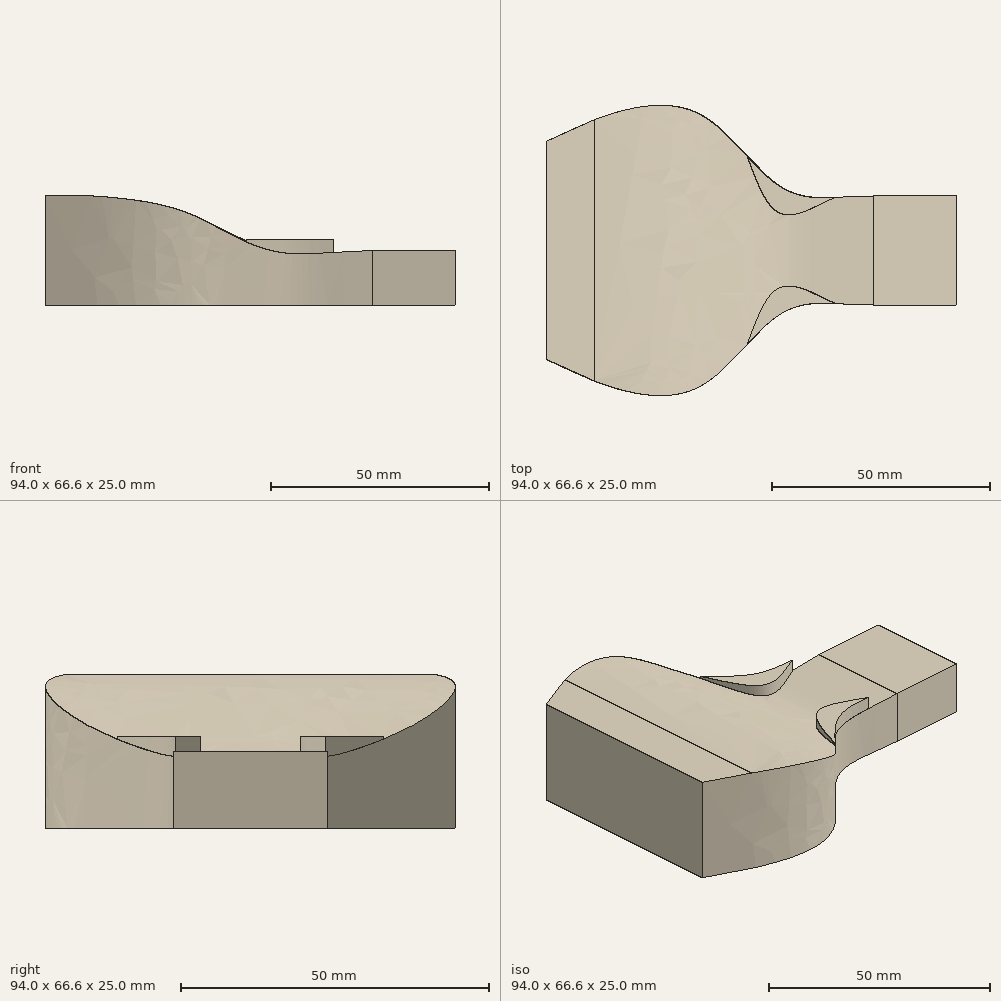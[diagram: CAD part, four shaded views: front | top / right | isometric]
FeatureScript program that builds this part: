
annotation { "Feature Type Name" : "Feature", "Feature Type Description" : "" }
export const myFeature = defineFeature(function(context is Context, id is Id, definition is map)
    precondition{}
    {
        {
            var Q0;
            Q0=qCreatedBy(makeId("Top.planeOp"),FACE);
            var sketch = newSketch(context, id + "F0", { "sketchPlane" : qUnion([Q0])});
            skLineSegment(sketch, "E0", {"start": v(-32.15, 0) * mm, "end": v(-32.15, 25) * mm});
            skLineSegment(sketch, "E1", {"start": v(42.85, 0) * mm, "end": v(42.85, 12.5) * mm});
            skFitSpline(sketch, "E2", {"points": [v(-32.15, 25) * mm, v(-16.91, 31.43) * mm, v(2.7, 31.43) * mm, v(22.53, 14.05) * mm, v(42.85, 12.5) * mm], "startDerivative": vector(94.79, 43.23) * mm, "endDerivative": vector(92.27, -1.18) * mm});
            skFitSpline(sketch, "E3.MirrorCS", {"points": [v(-32.15, -25) * mm, v(-16.91, -31.43) * mm, v(2.7, -31.43) * mm, v(22.53, -14.05) * mm, v(42.85, -12.5) * mm], "startDerivative": vector(94.79, -43.23) * mm, "endDerivative": vector(92.27, 1.18) * mm});
            skLineSegment(sketch, "E4.MirrorCS", {"start": v(-32.15, 0) * mm, "end": v(-32.15, -25) * mm});
            skLineSegment(sketch, "E5.MirrorCS", {"start": v(42.85, 0) * mm, "end": v(42.85, -12.5) * mm});
            skSolve(sketch);
        }
        {
            var Q0;
            Q0=makeQuery(id+"F0.imprint","IMPRINT",FACE,{"disambiguationData":[TD([[makeQuery(id+"F0.imprint","IMPRINT",EDGE,{"derivedFrom":sQuery(id+"F0.wireOp",EDGE,"E0")}),-1.0]])]});
            extrude(context, id + "F1", {"entities" : qUnion([Q0]), "depth" : 25 * mm});
        }
        {
            var Q0;
            Q0=qCreatedBy(makeId("Front.planeOp"),FACE);
            var sketch = newSketch(context, id + "F2", { "sketchPlane" : qUnion([Q0])});
            skLineSegment(sketch, "E6.0", {"start": v(-32.15, 25) * mm, "end": v(-32.15, 0) * mm});
            skLineSegment(sketch, "E7", {"start": v(42.85, 0) * mm, "end": v(42.85, 12.5) * mm});
            skFitSpline(sketch, "E8", {"points": [v(42.85, 12.5) * mm, v(30.39, 11.85) * mm, v(20.57, 12.29) * mm, v(10.27, 16.21) * mm, v(-3.97, 22.56) * mm, v(-32.15, 25) * mm], "startDerivative": vector(-65.38, -2.17) * mm, "endDerivative": vector(-72.27, -5.88) * mm});
            skLineSegment(sketch, "E9", {"start": v(42.85, 0) * mm, "end": v(-32.15, 0) * mm});
            skSolve(sketch);
        }
        {
            var Q0;
            Q0 = qSketchRegion(id + "F2", true);
            extrude(context, id + "F3", {"entities" : qUnion([Q0]), "operationType" : NewBodyOperationType.INTERSECT, "endBound" : BoundingType.SYMMETRIC, "depth" : 88.46 * mm});
        }
        {
            var Q0;
            Q0=qCreatedBy(makeId("Top.planeOp"),FACE);
            var sketch = newSketch(context, id + "F4", { "sketchPlane" : qUnion([Q0])});
            skFitSpline(sketch, "E10.0", {"points": [v(-32.15, 25) * mm, v(-25.07, 28.23) * mm, v(-18.53, 31.71) * mm, v(5.25, 36.39) * mm, v(20.78, 8.87) * mm, v(35.2, 12.6) * mm, v(42.85, 12.5) * mm]});
            skFitSpline(sketch, "E11", {"points": [v(-32.15, 25) * mm, v(-34, 32.96) * mm, v(-32.7, 43.34) * mm, v(-33.56, 51.35) * mm, v(-35.72, 58.05) * mm], "startDerivative": vector(-15.67, 34.06) * mm, "endDerivative": vector(-6.75, 15.63) * mm});
            skFitSpline(sketch, "E12", {"points": [v(-35.72, 58.05) * mm, v(-23.17, 60) * mm, v(-6.08, 53.94) * mm, v(5.39, 54.16) * mm], "startDerivative": vector(37.63, 12.7) * mm, "endDerivative": vector(35.9, 6.15) * mm});
            skFitSpline(sketch, "E13", {"points": [v(5.39, 54.16) * mm, v(7.98, 46.15) * mm, v(7.55, 40.1) * mm, v(5.39, 33.6) * mm, v(8.62, 26.19) * mm], "startDerivative": vector(12.12, -30.8) * mm, "endDerivative": vector(18.55, -28.53) * mm});
            skFitSpline(sketch, "E14.0", {"points": [v(42.85, 12.5) * mm, v(41.3, 12.52) * mm, v(38.23, 12.4) * mm, v(34.4, 12.15) * mm, v(31.32, 12.1) * mm, v(29, 12.19) * mm, v(27.12, 12.45) * mm, v(25.63, 12.8) * mm, v(24.71, 13.09) * mm, v(23.99, 13.36) * mm, v(23.28, 13.67) * mm, v(22.43, 14.1) * mm, v(21.46, 14.67) * mm, v(20.53, 15.32) * mm, v(19.64, 16) * mm, v(18.48, 16.98) * mm, v(17.11, 18.26) * mm, v(15.55, 19.85) * mm, v(13.54, 22) * mm, v(11.56, 24.15) * mm, v(9.55, 26.2) * mm, v(8, 27.67) * mm, v(6.4, 29.05) * mm, v(4.97, 30.1) * mm, v(3.75, 30.87) * mm, v(2.5, 31.56) * mm, v(1.2, 32.12) * mm, v(-0.18, 32.56) * mm, v(-1.25, 32.83) * mm, v(-2.35, 33.03) * mm, v(-3.81, 33.23) * mm, v(-5.3, 33.31) * mm, v(-6.81, 33.3) * mm, v(-8.34, 33.21) * mm, v(-10.23, 33) * mm, v(-12.47, 32.6) * mm, v(-14.7, 32.08) * mm, v(-16.9, 31.45) * mm, v(-19.1, 30.74) * mm, v(-20.54, 30.2) * mm, v(-21.26, 29.9) * mm]});
            skPoint(sketch, "E15.orphan", {"position": v(42.85, 12.5) * mm});
            skSolve(sketch);
        }
        {
            var Q0;
            Q0=makeQuery(id+"F4.imprint","IMPRINT",FACE,{"disambiguationData":[TD([[makeQuery(id+"F4.imprint","IMPRINT",EDGE,{"derivedFrom":sQuery(id+"F4.wireOp",EDGE,"E10.0")}),1.0]])]});
            extrude(context, id + "F5", {"entities" : qUnion([Q0]), "depth" : 15 * mm});
        }
        {
            var Q0;
            Q0=makeQuery(id+"F5.opExtrude","SWEPT_BODY",BODY,{"disambiguationData":[OSD([sQuery(id+"F4.wireOp",EDGE,"E10.0"),sQuery(id+"F4.wireOp",EDGE,"E11"),sQuery(id+"F4.wireOp",EDGE,"E12"),sQuery(id+"F4.wireOp",EDGE,"E13"),sQuery(id+"F4.wireOp",EDGE,"E14.0")])]});
            var Q1;
            Q1=qCreatedBy(makeId("Front.planeOp"),FACE);
            mirror(context, id + "F6", {"entities" : qUnion([Q0]), "mirrorPlane" : qUnion([Q1])});
        }
        {
            var Q0;
            Q0=makeQuery(id+"F1.opExtrude","SWEPT_BODY",BODY,{"disambiguationData":[OSD([sQuery(id+"F0.wireOp",EDGE,"E0"),sQuery(id+"F0.wireOp",EDGE,"E1"),sQuery(id+"F0.wireOp",EDGE,"E2"),sQuery(id+"F0.wireOp",EDGE,"E3.MirrorCS"),sQuery(id+"F0.wireOp",EDGE,"E4.MirrorCS"),sQuery(id+"F0.wireOp",EDGE,"E5.MirrorCS")])]});
            var Q1;
            Q1=makeQuery(id+"F5.opExtrude","SWEPT_BODY",BODY,{"disambiguationData":[OSD([sQuery(id+"F4.wireOp",EDGE,"E10.0"),sQuery(id+"F4.wireOp",EDGE,"E11"),sQuery(id+"F4.wireOp",EDGE,"E12"),sQuery(id+"F4.wireOp",EDGE,"E13"),sQuery(id+"F4.wireOp",EDGE,"E14.0")])]});
            booleanBodies(context, id + "F7", {"operationType" : BooleanOperationType.UNION, "tools" : qUnion([Q0, Q1])});
        }
        {
            var Q0;
            Q0=makeQuery(id+"F6.opPattern","COPY",BODY,{"derivedFrom":makeQuery(id+"F5.opExtrude","SWEPT_BODY",BODY,{"disambiguationData":[OSD([sQuery(id+"F4.wireOp",EDGE,"E10.0"),sQuery(id+"F4.wireOp",EDGE,"E11"),sQuery(id+"F4.wireOp",EDGE,"E12"),sQuery(id+"F4.wireOp",EDGE,"E13"),sQuery(id+"F4.wireOp",EDGE,"E14.0")])]}),"instanceName":"1"});
            var Q1;
            Q1=makeQuery(id+"F1.opExtrude","SWEPT_BODY",BODY,{"disambiguationData":[OSD([sQuery(id+"F0.wireOp",EDGE,"E0"),sQuery(id+"F0.wireOp",EDGE,"E1"),sQuery(id+"F0.wireOp",EDGE,"E2"),sQuery(id+"F0.wireOp",EDGE,"E3.MirrorCS"),sQuery(id+"F0.wireOp",EDGE,"E4.MirrorCS"),sQuery(id+"F0.wireOp",EDGE,"E5.MirrorCS")])]});
            booleanBodies(context, id + "F8", {"operationType" : BooleanOperationType.UNION, "tools" : qUnion([Q0, Q1])});
        }
        {
            var Q0;
            Q0=makeQuery(id+"F1.opExtrude","SWEPT_FACE",FACE,{"disambiguationData":[OSD([sQuery(id+"F0.wireOp",EDGE,"E1"),sQuery(id+"F0.wireOp",EDGE,"E5.MirrorCS")])]});
            extrude(context, id + "F9", {"entities" : qUnion([Q0]), "operationType" : NewBodyOperationType.ADD, "depth" : 19.04 * mm});
        }
        {
            var Q0;
            {var subQ0=sQuery(id+"F0.wireOp",EDGE,"E5.MirrorCS");var subQ1=sQuery(id+"F0.wireOp",EDGE,"E1");var subQ2=makeQuery(id+"F5.opExtrude","CAP_FACE",FACE,{"disambiguationData":[OSD([sQuery(id+"F4.wireOp",EDGE,"E10.0"),sQuery(id+"F4.wireOp",EDGE,"E11"),sQuery(id+"F4.wireOp",EDGE,"E12"),sQuery(id+"F4.wireOp",EDGE,"E13"),sQuery(id+"F4.wireOp",EDGE,"E14.0")])],"isStart":true});Q0=makeQuery(id+"F9.boolean.opBoolean","MERGE",FACE,{"derivedFrom":[makeQuery(id+"F8.opBoolean","MERGE",FACE,{"derivedFrom":[makeQuery(id+"F6.opPattern","COPY",FACE,{"derivedFrom":subQ2,"instanceName":"1"}),makeQuery(id+"F7.opBoolean","MERGE",FACE,{"derivedFrom":[makeQuery(id+"F1.opExtrude","CAP_FACE",FACE,{"disambiguationData":[OSD([sQuery(id+"F0.wireOp",EDGE,"E0"),subQ1,sQuery(id+"F0.wireOp",EDGE,"E2"),sQuery(id+"F0.wireOp",EDGE,"E3.MirrorCS"),sQuery(id+"F0.wireOp",EDGE,"E4.MirrorCS"),subQ0])],"isStart":true}),subQ2]})]}),makeQuery(id+"F9.opExtrude","SWEPT_FACE",FACE,{"disambiguationData":[OSD([subQ1,subQ0])]})]});}
            shell(context, id + "F10", {"entities" : qUnion([Q0]), "thickness" : 2.5 * mm});
        }
    });
